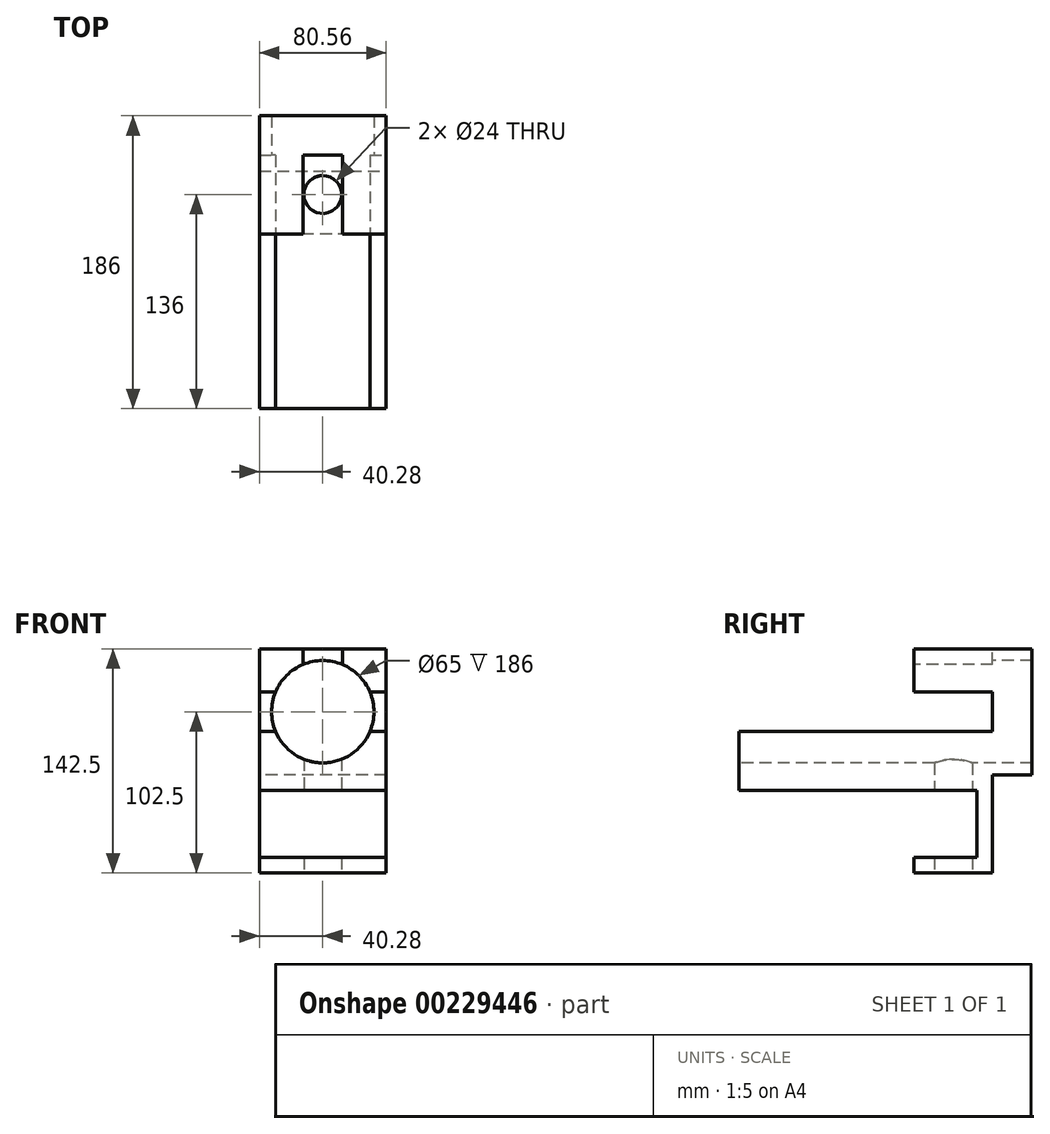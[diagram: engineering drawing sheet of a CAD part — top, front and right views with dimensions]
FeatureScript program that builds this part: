
annotation { "Feature Type Name" : "Feature", "Feature Type Description" : "" }
export const myFeature = defineFeature(function(context is Context, id is Id, definition is map)
    precondition{}
    {
        {
            var Q0;
            Q0=qCreatedBy(makeId("Front.planeOp"),FACE);
            var sketch = newSketch(context, id + "F0", { "sketchPlane" : qUnion([Q0])});
            skLineSegment(sketch, "E0.bottom", {"start": v(40.28, 40) * mm, "end": v(-40.28, 40) * mm});
            skLineSegment(sketch, "E0.top", {"start": v(40.28, -40) * mm, "end": v(-40.28, -40) * mm});
            skLineSegment(sketch, "E0.left", {"start": v(40.28, 40) * mm, "end": v(40.28, -40) * mm});
            skLineSegment(sketch, "E0.right", {"start": v(-40.28, 40) * mm, "end": v(-40.28, -40) * mm});
            skPoint(sketch, "E0.middle", {"position": v(0, 0) * mm});
            skSolve(sketch);
        }
        {
            var Q0;
            Q0=makeQuery(id+"F0.imprint","IMPRINT",FACE,{"disambiguationData":[TD([[makeQuery(id+"F0.imprint","IMPRINT",EDGE,{"derivedFrom":sQuery(id+"F0.wireOp",EDGE,"E0.bottom")}),1.0]])]});
            extrude(context, id + "F1", {"entities" : qUnion([Q0]), "endBound" : BoundingType.SYMMETRIC, "depth" : 350 * mm});
        }
        {
            var Q0;
            Q0=makeQuery(id+"F1.opExtrude","CAP_FACE",FACE,{"disambiguationData":[OSD([sQuery(id+"F0.wireOp",EDGE,"E0.bottom"),sQuery(id+"F0.wireOp",EDGE,"E0.top"),sQuery(id+"F0.wireOp",EDGE,"E0.left"),sQuery(id+"F0.wireOp",EDGE,"E0.right")])],"isStart":false});
            var sketch = newSketch(context, id + "F2", { "sketchPlane" : qUnion([Q0])});
            skCircle(sketch, "E1", {"center": v(0, 0) * mm, "radius": 32.5 * mm});
            skSolve(sketch);
        }
        {
            var Q0;
            Q0=makeQuery(id+"F2.imprint","IMPRINT",FACE,{"disambiguationData":[TD([[makeQuery(id+"F2.imprint","IMPRINT",EDGE,{"derivedFrom":sQuery(id+"F2.wireOp",EDGE,"E1")}),1.0]])]});
            extrude(context, id + "F3", {"entities" : qUnion([Q0]), "operationType" : NewBodyOperationType.REMOVE, "oppositeDirection" : true, "depth" : 300 * mm});
        }
        {
            var Q0;
            Q0=makeQuery(id+"F1.opExtrude","SWEPT_FACE",FACE,{"disambiguationData":[OSD([sQuery(id+"F0.wireOp",EDGE,"E0.bottom")])]});
            var sketch = newSketch(context, id + "F4", { "sketchPlane" : qUnion([Q0])});
            skLineSegment(sketch, "E2.bottom", {"start": v(12.5, 150) * mm, "end": v(-12.5, 150) * mm});
            skLineSegment(sketch, "E2.top", {"start": v(12.5, -150) * mm, "end": v(-12.5, -150) * mm});
            skLineSegment(sketch, "E2.left", {"start": v(12.5, 150) * mm, "end": v(12.5, -150) * mm});
            skLineSegment(sketch, "E2.right", {"start": v(-12.5, 150) * mm, "end": v(-12.5, -150) * mm});
            skPoint(sketch, "E2.middle", {"position": v(0, 0) * mm});
            skSolve(sketch);
        }
        {
            var Q0;
            Q0=makeQuery(id+"F4.imprint","IMPRINT",FACE,{"disambiguationData":[TD([[makeQuery(id+"F4.imprint","IMPRINT",EDGE,{"derivedFrom":sQuery(id+"F4.wireOp",EDGE,"E2.bottom")}),1.0]])]});
            extrude(context, id + "F5", {"entities" : qUnion([Q0]), "operationType" : NewBodyOperationType.REMOVE, "endBound" : BoundingType.THROUGH_ALL, "oppositeDirection" : true, "depth" : 25 * mm});
        }
        {
            var Q0;
            Q0=makeQuery(id+"F1.opExtrude","SWEPT_FACE",FACE,{"disambiguationData":[OSD([sQuery(id+"F0.wireOp",EDGE,"E0.left")])]});
            var sketch = newSketch(context, id + "F6", { "sketchPlane" : qUnion([Q0])});
            skLineSegment(sketch, "E3.bottom", {"start": v(150, 12.5) * mm, "end": v(-150, 12.5) * mm});
            skLineSegment(sketch, "E3.top", {"start": v(150, -12.5) * mm, "end": v(-150, -12.5) * mm});
            skLineSegment(sketch, "E3.left", {"start": v(150, 12.5) * mm, "end": v(150, -12.5) * mm});
            skLineSegment(sketch, "E3.right", {"start": v(-150, 12.5) * mm, "end": v(-150, -12.5) * mm});
            skPoint(sketch, "E3.middle", {"position": v(0, 0) * mm});
            skSolve(sketch);
        }
        {
            var Q0;
            Q0=makeQuery(id+"F6.imprint","IMPRINT",FACE,{"disambiguationData":[TD([[makeQuery(id+"F6.imprint","IMPRINT",EDGE,{"derivedFrom":sQuery(id+"F6.wireOp",EDGE,"E3.bottom")}),1.0]])]});
            extrude(context, id + "F7", {"entities" : qUnion([Q0]), "operationType" : NewBodyOperationType.REMOVE, "endBound" : BoundingType.THROUGH_ALL, "oppositeDirection" : true, "depth" : 25 * mm});
        }
        {
            var Q0;
            Q0=makeQuery(id+"F1.opExtrude","SWEPT_FACE",FACE,{"disambiguationData":[OSD([sQuery(id+"F0.wireOp",EDGE,"E0.top")])]});
            var sketch = newSketch(context, id + "F8", { "sketchPlane" : qUnion([Q0])});
            skLineSegment(sketch, "E4.bottom", {"start": v(-40.28, -175) * mm, "end": v(40.28, -175) * mm});
            skLineSegment(sketch, "E4.top", {"start": v(-40.28, -223.41) * mm, "end": v(40.28, -223.41) * mm});
            skLineSegment(sketch, "E4.left", {"start": v(-40.28, -175) * mm, "end": v(-40.28, -223.41) * mm});
            skLineSegment(sketch, "E4.right", {"start": v(40.28, -175) * mm, "end": v(40.28, -223.41) * mm});
            skSolve(sketch);
        }
        {
            var Q0;
            Q0=makeQuery(id+"F8.imprint","IMPRINT",FACE,{"disambiguationData":[TD([[makeQuery(id+"F8.imprint","IMPRINT",EDGE,{"derivedFrom":sQuery(id+"F8.wireOp",EDGE,"E4.bottom")}),1.0]])]});
            extrude(context, id + "F9", {"entities" : qUnion([Q0]), "operationType" : NewBodyOperationType.ADD, "oppositeDirection" : true, "depth" : 25 * mm});
        }
        {
            var Q0;
            Q0=makeQuery(id+"F9.opExtrude","CAP_FACE",FACE,{"disambiguationData":[OSD([sQuery(id+"F8.wireOp",EDGE,"E4.bottom"),sQuery(id+"F8.wireOp",EDGE,"E4.top"),sQuery(id+"F8.wireOp",EDGE,"E4.left"),sQuery(id+"F8.wireOp",EDGE,"E4.right")])],"isStart":false});
            var sketch = newSketch(context, id + "F10", { "sketchPlane" : qUnion([Q0])});
            skCircle(sketch, "E5", {"center": v(0, 199.2) * mm, "radius": 14.1 * mm});
            skLineSegment(sketch, "E6", {"start": v(-40.28, 223.41) * mm, "end": v(40.28, 175) * mm, "construction": true});
            skLineSegment(sketch, "E7", {"start": v(40.28, 175) * mm, "end": v(-40.28, 175) * mm, "construction": true});
            skLineSegment(sketch, "E8", {"start": v(-40.28, 175) * mm, "end": v(40.28, 223.41) * mm, "construction": true});
            skSolve(sketch);
        }
        {
            var Q0;
            Q0=makeQuery(id+"F10.imprint","IMPRINT",FACE,{"disambiguationData":[TD([[makeQuery(id+"F10.imprint","IMPRINT",EDGE,{"derivedFrom":sQuery(id+"F10.wireOp",EDGE,"E5")}),1.0]])]});
            extrude(context, id + "F11", {"entities" : qUnion([Q0]), "operationType" : NewBodyOperationType.REMOVE, "endBound" : BoundingType.THROUGH_ALL, "oppositeDirection" : true, "depth" : 25 * mm});
        }
        {
            var Q0;
            Q0=qCreatedBy(makeId("Top.planeOp"),FACE);
            cPlane(context, id + "F12", {"entities" : qUnion([Q0]), "cplaneType" : CPlaneType.OFFSET, "offset" : 40 * mm, "oppositeDirection" : true, "width" : 150 * mm, "height" : 150 * mm});
        }
        {
            var Q0;
            Q0=qCreatedBy(id+"F12.planeOp",FACE);
            var sketch = newSketch(context, id + "F13", { "sketchPlane" : qUnion([Q0])});
            skLineSegment(sketch, "E9.0", {"start": v(-12.5, 150) * mm, "end": v(12.5, 150) * mm, "construction": true});
            skLineSegment(sketch, "E10.bottom", {"start": v(-40.28, 150) * mm, "end": v(40.28, 150) * mm});
            skLineSegment(sketch, "E10.top", {"start": v(-40.28, 100) * mm, "end": v(40.28, 100) * mm});
            skLineSegment(sketch, "E10.left", {"start": v(-40.28, 150) * mm, "end": v(-40.28, 100) * mm});
            skLineSegment(sketch, "E10.right", {"start": v(40.28, 150) * mm, "end": v(40.28, 100) * mm});
            skSolve(sketch);
        }
        {
            var Q0;
            Q0=makeQuery(id+"F13.imprint","IMPRINT",FACE,{"disambiguationData":[TD([[makeQuery(id+"F13.imprint","IMPRINT",EDGE,{"derivedFrom":sQuery(id+"F13.wireOp",EDGE,"E10.bottom")}),-1.0]])]});
            extrude(context, id + "F14", {"entities" : qUnion([Q0]), "operationType" : NewBodyOperationType.ADD, "depth" : 10 * mm, "hasSecondDirection" : true, "secondDirectionOppositeDirection" : true, "secondDirectionDepth" : 62.5 * mm});
        }
        {
            var Q0;
            Q0=makeQuery(id+"F9.opExtrude","CAP_FACE",FACE,{"disambiguationData":[OSD([sQuery(id+"F8.wireOp",EDGE,"E4.bottom"),sQuery(id+"F8.wireOp",EDGE,"E4.top"),sQuery(id+"F8.wireOp",EDGE,"E4.left"),sQuery(id+"F8.wireOp",EDGE,"E4.right")])],"isStart":false});
            extrude(context, id + "F15", {"entities" : qUnion([Q0]), "operationType" : NewBodyOperationType.REMOVE, "oppositeDirection" : true, "depth" : 25 * mm});
        }
        {
            var Q0;
            Q0=makeQuery(id+"F14.boolean.opBoolean","MERGE",FACE,{"derivedFrom":[makeQuery(id+"F9.boolean.opBoolean","MERGE",FACE,{"derivedFrom":[makeQuery(id+"F1.opExtrude","SWEPT_FACE",FACE,{"disambiguationData":[OSD([sQuery(id+"F0.wireOp",EDGE,"E0.left")])]}),makeQuery(id+"F9.opExtrude","SWEPT_FACE",FACE,{"disambiguationData":[OSD([sQuery(id+"F8.wireOp",EDGE,"E4.right")])]})]}),makeQuery(id+"F14.opExtrude","SWEPT_FACE",FACE,{"disambiguationData":[OSD([sQuery(id+"F13.wireOp",EDGE,"E10.right")])]})]});
            var sketch = newSketch(context, id + "F16", { "sketchPlane" : qUnion([Q0])});
            skLineSegment(sketch, "E11.bottom", {"start": v(-178.8, 79.57) * mm, "end": v(100, 79.57) * mm});
            skLineSegment(sketch, "E11.top", {"start": v(-178.8, -116.95) * mm, "end": v(100, -116.95) * mm});
            skLineSegment(sketch, "E11.left", {"start": v(-178.8, 79.57) * mm, "end": v(-178.8, -116.95) * mm});
            skLineSegment(sketch, "E11.right", {"start": v(100, 79.57) * mm, "end": v(100, -116.95) * mm});
            skSolve(sketch);
        }
        {
            var Q0;
            {var subQ1=sQuery(id+"F16.wireOp",EDGE,"E11.bottom");Q0=makeQuery(id+"F16.imprint","IMPRINT",FACE,{"disambiguationData":[TD([[makeQuery(id+"F16.imprint","IMPRINT",EDGE,{"derivedFrom":subQ1}),-1.0]])]});}
            var Q1;
            {var subQ2=sQuery(id+"F0.wireOp",EDGE,"E0.left");var subQ9=makeQuery(id+"F1.opExtrude","CAP_EDGE",EDGE,{"disambiguationData":[OSD([subQ2])],"isStart":false});Q1=makeQuery(id+"F16.imprint","IMPRINT",FACE,{"disambiguationData":[TD([[makeQuery(id+"F16.imprint","IMPRINT",EDGE,{"derivedFrom":subQ9}),1.0]])]});}
            extrude(context, id + "F17", {"entities" : qUnion([Q0, Q1]), "operationType" : NewBodyOperationType.REMOVE, "endBound" : BoundingType.THROUGH_ALL, "oppositeDirection" : true, "depth" : 25 * mm});
        }
        {
            var Q0;
            Q0=makeQuery(id+"F15.boolean.opBoolean","MERGE",FACE,{"derivedFrom":[makeQuery(id+"F1.opExtrude","CAP_FACE",FACE,{"disambiguationData":[OSD([sQuery(id+"F0.wireOp",EDGE,"E0.bottom"),sQuery(id+"F0.wireOp",EDGE,"E0.top"),sQuery(id+"F0.wireOp",EDGE,"E0.left"),sQuery(id+"F0.wireOp",EDGE,"E0.right")])],"isStart":true}),makeQuery(id+"F15.opExtrude","SWEPT_FACE",FACE,{"disambiguationData":[OSD([sQuery(id+"F8.wireOp",EDGE,"E4.bottom")])]})]});
            var sketch = newSketch(context, id + "F18", { "sketchPlane" : qUnion([Q0])});
            skCircle(sketch, "E12", {"center": v(0, 0) * mm, "radius": 32.5 * mm});
            skSolve(sketch);
        }
        {
            var Q0;
            Q0=makeQuery(id+"F18.imprint","IMPRINT",FACE,{"disambiguationData":[TD([[makeQuery(id+"F18.imprint","IMPRINT",EDGE,{"derivedFrom":sQuery(id+"F18.wireOp",EDGE,"E12")}),1.0]])]});
            extrude(context, id + "F19", {"entities" : qUnion([Q0]), "operationType" : NewBodyOperationType.REMOVE, "endBound" : BoundingType.THROUGH_ALL, "oppositeDirection" : true, "depth" : 25 * mm});
        }
        {
            var Q0;
            Q0=makeQuery(id+"F14.boolean.opBoolean","MERGE",FACE,{"derivedFrom":[makeQuery(id+"F9.boolean.opBoolean","MERGE",FACE,{"derivedFrom":[makeQuery(id+"F1.opExtrude","SWEPT_FACE",FACE,{"disambiguationData":[OSD([sQuery(id+"F0.wireOp",EDGE,"E0.left")])]}),makeQuery(id+"F9.opExtrude","SWEPT_FACE",FACE,{"disambiguationData":[OSD([sQuery(id+"F8.wireOp",EDGE,"E4.right")])]})]}),makeQuery(id+"F14.opExtrude","SWEPT_FACE",FACE,{"disambiguationData":[OSD([sQuery(id+"F13.wireOp",EDGE,"E10.right")])]})]});
            var sketch = newSketch(context, id + "F20", { "sketchPlane" : qUnion([Q0])});
            skLineSegment(sketch, "E13.bottom", {"start": v(96.9, -50) * mm, "end": v(140, -50) * mm});
            skLineSegment(sketch, "E13.top", {"start": v(96.9, -92.5) * mm, "end": v(140, -92.5) * mm});
            skLineSegment(sketch, "E13.left", {"start": v(96.9, -50) * mm, "end": v(96.9, -92.5) * mm});
            skLineSegment(sketch, "E13.right", {"start": v(140, -50) * mm, "end": v(140, -92.5) * mm});
            skSolve(sketch);
        }
        {
            var Q0;
            {var subQ0=sQuery(id+"F20.wireOp",EDGE,"E13.left");Q0=makeQuery(id+"F20.imprint","IMPRINT",FACE,{"disambiguationData":[TD([[makeQuery(id+"F20.imprint","IMPRINT",EDGE,{"derivedFrom":subQ0}),1.0]])]});}
            var Q1;
            {var subQ0=sQuery(id+"F20.wireOp",EDGE,"E13.right");Q1=makeQuery(id+"F20.imprint","IMPRINT",FACE,{"disambiguationData":[TD([[makeQuery(id+"F20.imprint","IMPRINT",EDGE,{"derivedFrom":subQ0}),-1.0]])]});}
            extrude(context, id + "F21", {"entities" : qUnion([Q0, Q1]), "operationType" : NewBodyOperationType.REMOVE, "endBound" : BoundingType.THROUGH_ALL, "oppositeDirection" : true, "depth" : 25 * mm});
        }
        {
            var Q0;
            Q0=makeQuery(id+"F14.opExtrude","CAP_FACE",FACE,{"disambiguationData":[OSD([sQuery(id+"F13.wireOp",EDGE,"E10.bottom"),sQuery(id+"F13.wireOp",EDGE,"E10.top"),sQuery(id+"F13.wireOp",EDGE,"E10.left"),sQuery(id+"F13.wireOp",EDGE,"E10.right")])],"isStart":true});
            var sketch = newSketch(context, id + "F22", { "sketchPlane" : qUnion([Q0])});
            skLineSegment(sketch, "E14", {"start": v(-40.28, -100) * mm, "end": v(40.28, -150) * mm, "construction": true});
            skLineSegment(sketch, "E15", {"start": v(40.28, -150) * mm, "end": v(40.28, -100) * mm, "construction": true});
            skLineSegment(sketch, "E16", {"start": v(40.28, -100) * mm, "end": v(-40.28, -150) * mm, "construction": true});
            skPoint(sketch, "E17", {"position": v(0, -125) * mm});
            skCircle(sketch, "E18", {"center": v(0, -125) * mm, "radius": 12 * mm});
            skSolve(sketch);
        }
        {
            var Q0;
            Q0=makeQuery(id+"F22.imprint","IMPRINT",FACE,{"disambiguationData":[TD([[makeQuery(id+"F22.imprint","IMPRINT",EDGE,{"derivedFrom":sQuery(id+"F22.wireOp",EDGE,"E18")}),1.0]])]});
            extrude(context, id + "F23", {"entities" : qUnion([Q0]), "operationType" : NewBodyOperationType.REMOVE, "endBound" : BoundingType.THROUGH_ALL, "oppositeDirection" : true, "depth" : 25 * mm});
        }
        {
            var Q0;
            {var subQ2=makeQuery(id+"F1.opExtrude","SWEPT_FACE",FACE,{"disambiguationData":[OSD([sQuery(id+"F0.wireOp",EDGE,"E0.right")])]});var subQ5=sQuery(id+"F6.wireOp",EDGE,"E3.bottom");var subQ6=sQuery(id+"F16.wireOp",EDGE,"E11.right");Q0=makeQuery(id+"F17.boolean.opBoolean","COPY",FACE,{"disambiguationData":[TD([subQ2])],"derivedFrom":makeQuery(id+"F17.opExtrude","SWEPT_FACE",FACE,{"disambiguationData":[OSD([subQ6]),TDD([makeQuery(id+"F16.imprint","IMPRINT",EDGE,{"disambiguationData":[TD([[makeQuery(id+"F16.imprint","INTERSECT",VERTEX,{"derivedFrom":[sQuery(id+"F16.wireOp",EDGE,"E11.bottom"),subQ6]}),-1.0]])],"derivedFrom":subQ6}),makeQuery(id+"F16.imprint","IMPRINT",EDGE,{"disambiguationData":[TD([[makeQuery(id+"F16.imprint","INTERSECT",VERTEX,{"derivedFrom":[makeQuery(id+"F7.boolean.opBoolean","COPY",EDGE,{"derivedFrom":makeQuery(id+"F7.opExtrude","CAP_EDGE",EDGE,{"disambiguationData":[OSD([subQ5])],"isStart":true})}),subQ6]}),1.0]])],"derivedFrom":subQ6})])]})});}
            var Q1;
            {var subQ3=sQuery(id+"F0.wireOp",EDGE,"E0.left");var subQ4=makeQuery(id+"F1.opExtrude","SWEPT_FACE",FACE,{"disambiguationData":[OSD([subQ3])]});var subQ6=sQuery(id+"F6.wireOp",EDGE,"E3.bottom");var subQ7=sQuery(id+"F16.wireOp",EDGE,"E11.right");Q1=makeQuery(id+"F17.boolean.opBoolean","COPY",FACE,{"disambiguationData":[TD([subQ4])],"derivedFrom":makeQuery(id+"F17.opExtrude","SWEPT_FACE",FACE,{"disambiguationData":[OSD([subQ7]),TDD([makeQuery(id+"F16.imprint","IMPRINT",EDGE,{"disambiguationData":[TD([[makeQuery(id+"F16.imprint","INTERSECT",VERTEX,{"derivedFrom":[sQuery(id+"F16.wireOp",EDGE,"E11.bottom"),subQ7]}),-1.0]])],"derivedFrom":subQ7}),makeQuery(id+"F16.imprint","IMPRINT",EDGE,{"disambiguationData":[TD([[makeQuery(id+"F16.imprint","INTERSECT",VERTEX,{"derivedFrom":[makeQuery(id+"F7.boolean.opBoolean","COPY",EDGE,{"derivedFrom":makeQuery(id+"F7.opExtrude","CAP_EDGE",EDGE,{"disambiguationData":[OSD([subQ6])],"isStart":true})}),subQ7]}),1.0]])],"derivedFrom":subQ7})])]})});}
            var Q2;
            {var subQ0=sQuery(id+"F13.wireOp",EDGE,"E10.right");var subQ7=sQuery(id+"F2.wireOp",EDGE,"E1");var subQ9=makeQuery(id+"F3.boolean.opBoolean","COPY",FACE,{"derivedFrom":makeQuery(id+"F3.opExtrude","SWEPT_FACE",FACE,{"disambiguationData":[OSD([subQ7])]})});var subQ14=sQuery(id+"F6.wireOp",EDGE,"E3.top");var subQ16=sQuery(id+"F13.wireOp",EDGE,"E10.top");var subQ19=sQuery(id+"F16.wireOp",EDGE,"E11.right");var subQ20=makeQuery(id+"F16.imprint","INTERSECT",VERTEX,{"derivedFrom":[makeQuery(id+"F14.opExtrude","CAP_EDGE",EDGE,{"disambiguationData":[OSD([subQ0])],"isStart":true}),subQ19]});var subQ22=makeQuery(id+"F14.opExtrude","SWEPT_FACE",FACE,{"disambiguationData":[OSD([subQ16])]});Q2=makeQuery(id+"F21.boolean.opBoolean","SPLIT",FACE,{"disambiguationData":[TD([subQ9])],"derivedFrom":makeQuery(id+"F17.boolean.opBoolean","MERGE",FACE,{"derivedFrom":[subQ22,makeQuery(id+"F17.opExtrude","SWEPT_FACE",FACE,{"disambiguationData":[OSD([subQ19]),TDD([makeQuery(id+"F16.imprint","IMPRINT",EDGE,{"disambiguationData":[TD([[makeQuery(id+"F16.imprint","INTERSECT",VERTEX,{"derivedFrom":[makeQuery(id+"F7.boolean.opBoolean","COPY",EDGE,{"derivedFrom":makeQuery(id+"F7.opExtrude","CAP_EDGE",EDGE,{"disambiguationData":[OSD([subQ14])],"isStart":true})}),subQ19]}),-1.0]])],"derivedFrom":subQ19}),makeQuery(id+"F16.imprint","IMPRINT",EDGE,{"disambiguationData":[TD([[subQ20,1.0]])],"derivedFrom":subQ19}),makeQuery(id+"F16.imprint","IMPRINT",EDGE,{"disambiguationData":[TD([[subQ20,-1.0]])],"derivedFrom":subQ19})])]})]})});}
            extrude(context, id + "F24", {"entities" : qUnion([Q0, Q1, Q2]), "operationType" : NewBodyOperationType.ADD, "depth" : 111 * mm});
        }
    });
